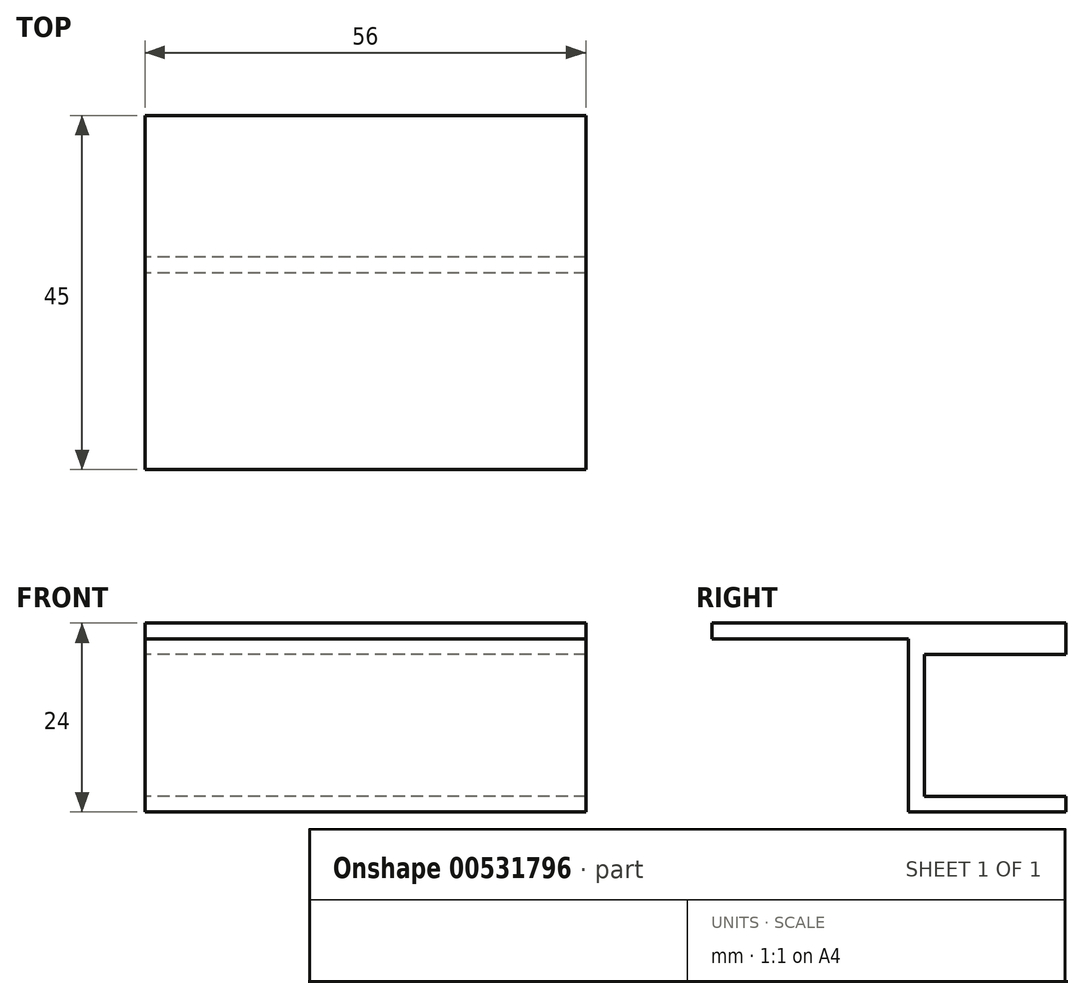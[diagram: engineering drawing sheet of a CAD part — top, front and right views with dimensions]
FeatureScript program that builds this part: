
annotation { "Feature Type Name" : "Feature", "Feature Type Description" : "" }
export const myFeature = defineFeature(function(context is Context, id is Id, definition is map)
    precondition{}
    {
        {
            var Q0;
            Q0=qCreatedBy(makeId("Top.planeOp"),FACE);
            var sketch = newSketch(context, id + "F0", { "sketchPlane" : qUnion([Q0])});
            skLineSegment(sketch, "E0.bottom", {"start": v(28, 22.5) * mm, "end": v(-28, 22.5) * mm});
            skLineSegment(sketch, "E0.top", {"start": v(28, -22.5) * mm, "end": v(-28, -22.5) * mm});
            skLineSegment(sketch, "E0.left", {"start": v(28, 22.5) * mm, "end": v(28, -22.5) * mm});
            skLineSegment(sketch, "E0.right", {"start": v(-28, 22.5) * mm, "end": v(-28, -22.5) * mm});
            skPoint(sketch, "E0.middle", {"position": v(0, 0) * mm});
            skSolve(sketch);
        }
        {
            var Q0;
            Q0 = qSketchRegion(id + "F0", true);
            extrude(context, id + "F1", {"entities" : qUnion([Q0]), "depth" : 2 * mm, "offsetDistance" : 25 * mm});
        }
        {
            var Q0;
            Q0=makeQuery(id+"F1.opExtrude","CAP_FACE",FACE,{"disambiguationData":[OSD([sQuery(id+"F0.wireOp",EDGE,"E0.bottom"),sQuery(id+"F0.wireOp",EDGE,"E0.top"),sQuery(id+"F0.wireOp",EDGE,"E0.left"),sQuery(id+"F0.wireOp",EDGE,"E0.right")])],"isStart":true});
            var sketch = newSketch(context, id + "F2", { "sketchPlane" : qUnion([Q0])});
            skLineSegment(sketch, "E1.bottom", {"start": v(28, -22.5) * mm, "end": v(-28, -22.5) * mm});
            skLineSegment(sketch, "E1.top", {"start": v(28, -2.5) * mm, "end": v(-28, -2.5) * mm});
            skLineSegment(sketch, "E1.left", {"start": v(28, -22.5) * mm, "end": v(28, -2.5) * mm});
            skLineSegment(sketch, "E1.right", {"start": v(-28, -22.5) * mm, "end": v(-28, -2.5) * mm});
            skSolve(sketch);
        }
        {
            var Q0;
            Q0 = qSketchRegion(id + "F2", true);
            extrude(context, id + "F3", {"entities" : qUnion([Q0]), "operationType" : NewBodyOperationType.ADD, "depth" : 2 * mm, "offsetDistance" : 25 * mm});
        }
        {
            var Q0;
            Q0=makeQuery(id+"F3.opExtrude","CAP_FACE",FACE,{"disambiguationData":[OSD([sQuery(id+"F2.wireOp",EDGE,"E1.bottom"),sQuery(id+"F2.wireOp",EDGE,"E1.top"),sQuery(id+"F2.wireOp",EDGE,"E1.left"),sQuery(id+"F2.wireOp",EDGE,"E1.right")])],"isStart":false});
            var sketch = newSketch(context, id + "F4", { "sketchPlane" : qUnion([Q0])});
            skLineSegment(sketch, "E2.bottom", {"start": v(28, -2.5) * mm, "end": v(-28, -2.5) * mm});
            skLineSegment(sketch, "E2.top", {"start": v(28, -4.5) * mm, "end": v(-28, -4.5) * mm});
            skLineSegment(sketch, "E2.left", {"start": v(28, -2.5) * mm, "end": v(28, -4.5) * mm});
            skLineSegment(sketch, "E2.right", {"start": v(-28, -2.5) * mm, "end": v(-28, -4.5) * mm});
            skSolve(sketch);
        }
        {
            var Q0;
            Q0 = qSketchRegion(id + "F4", true);
            extrude(context, id + "F5", {"entities" : qUnion([Q0]), "operationType" : NewBodyOperationType.ADD, "depth" : 20 * mm, "offsetDistance" : 25 * mm});
        }
        {
            var Q0;
            Q0=makeQuery(id+"F5.opExtrude","SWEPT_FACE",FACE,{"disambiguationData":[OSD([sQuery(id+"F4.wireOp",EDGE,"E2.top")])]});
            var sketch = newSketch(context, id + "F6", { "sketchPlane" : qUnion([Q0])});
            skLineSegment(sketch, "E3.bottom", {"start": v(-28, -22) * mm, "end": v(28, -22) * mm});
            skLineSegment(sketch, "E3.top", {"start": v(-28, -20) * mm, "end": v(28, -20) * mm});
            skLineSegment(sketch, "E3.left", {"start": v(-28, -22) * mm, "end": v(-28, -20) * mm});
            skLineSegment(sketch, "E3.right", {"start": v(28, -22) * mm, "end": v(28, -20) * mm});
            skSolve(sketch);
        }
        {
            var Q0;
            Q0 = qSketchRegion(id + "F6", true);
            extrude(context, id + "F7", {"entities" : qUnion([Q0]), "operationType" : NewBodyOperationType.ADD, "depth" : 20 * mm, "offsetDistance" : 25 * mm});
        }
        {
            var Q0;
            Q0=makeQuery(id+"F3.boolean.opBoolean","MERGE",FACE,{"derivedFrom":[makeQuery(id+"F1.opExtrude","SWEPT_FACE",FACE,{"disambiguationData":[OSD([sQuery(id+"F0.wireOp",EDGE,"E0.bottom")])]}),makeQuery(id+"F3.opExtrude","SWEPT_FACE",FACE,{"disambiguationData":[OSD([sQuery(id+"F2.wireOp",EDGE,"E1.bottom")])]})]});
            cPlane(context, id + "F8", {"entities" : qUnion([Q0]), "cplaneType" : CPlaneType.OFFSET, "offset" : 0 * mm, "width" : 150 * mm, "height" : 150 * mm});
        }
        {
            var Q0;
            Q0=qCreatedBy(id+"F8.planeOp",FACE);
            var sketch = newSketch(context, id + "F9", { "sketchPlane" : qUnion([Q0])});
            skLineSegment(sketch, "E4.bottom", {"start": v(29.95, 4.16) * mm, "end": v(-39.67, 4.16) * mm});
            skLineSegment(sketch, "E4.top", {"start": v(29.95, -29.83) * mm, "end": v(-39.67, -29.83) * mm});
            skLineSegment(sketch, "E4.left", {"start": v(29.95, 4.16) * mm, "end": v(29.95, -29.83) * mm});
            skLineSegment(sketch, "E4.right", {"start": v(-39.67, 4.16) * mm, "end": v(-39.67, -29.83) * mm});
            skSolve(sketch);
        }
        {
            var Q0;
            Q0 = qSketchRegion(id + "F9", true);
            extrude(context, id + "F10", {"entities" : qUnion([Q0]), "operationType" : NewBodyOperationType.REMOVE, "depth" : 25 * mm, "offsetDistance" : 25 * mm});
        }
    });
